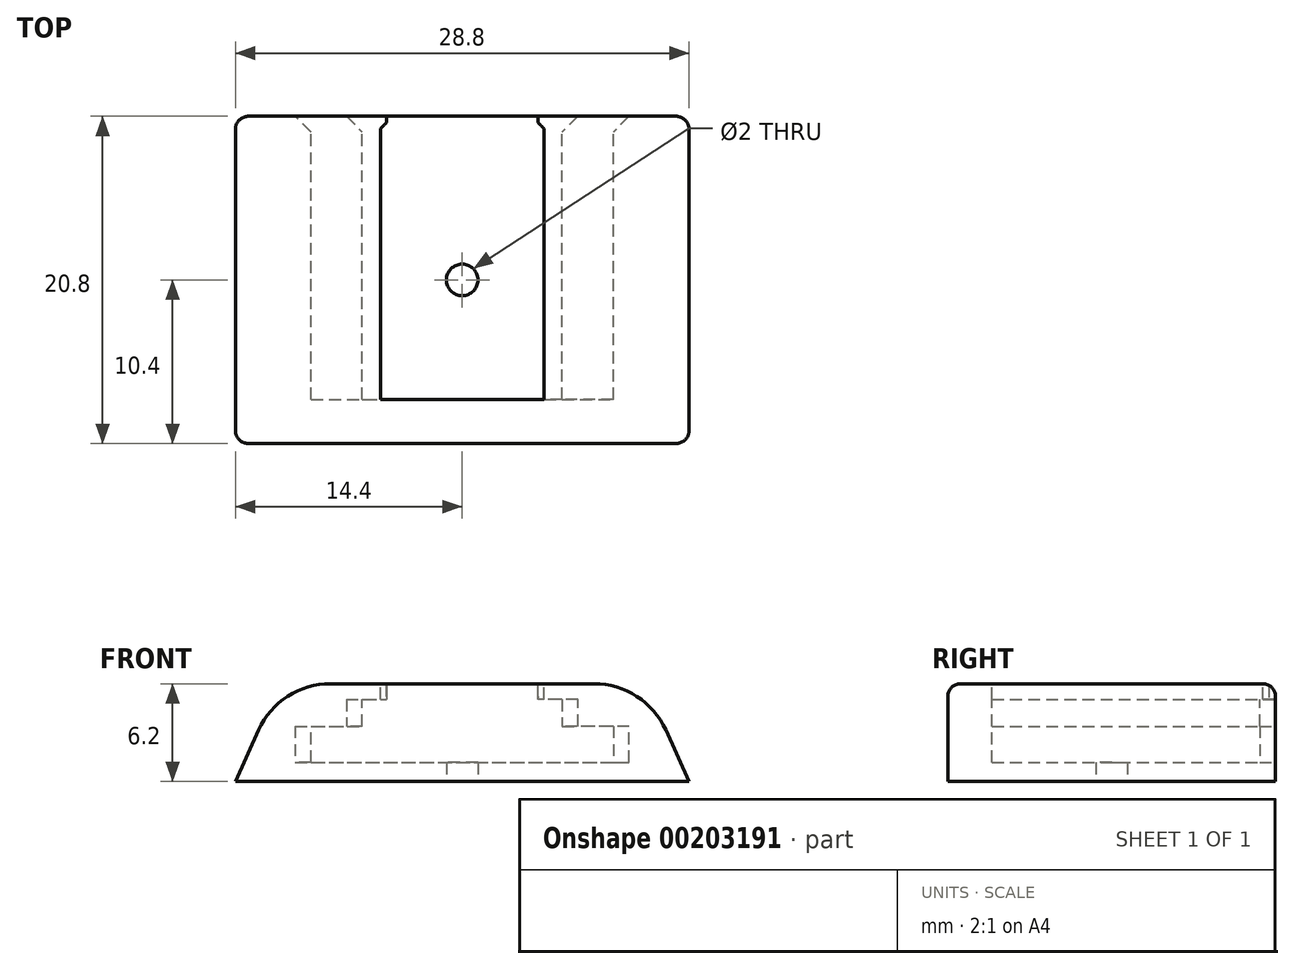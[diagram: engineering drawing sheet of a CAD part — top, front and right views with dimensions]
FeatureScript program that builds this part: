
annotation { "Feature Type Name" : "Feature", "Feature Type Description" : "" }
export const myFeature = defineFeature(function(context is Context, id is Id, definition is map)
    precondition{}
    {
        {
            var Q0;
            Q0=qCreatedBy(makeId("Front.planeOp"),FACE);
            var sketch = newSketch(context, id + "F0", { "sketchPlane" : qUnion([Q0])});
            skLineSegment(sketch, "E0", {"start": v(0, -5) * mm, "end": v(-9.6, -5) * mm});
            skLineSegment(sketch, "E1", {"start": v(-9.6, -5) * mm, "end": v(-9.6, -2.7) * mm});
            skLineSegment(sketch, "E2", {"start": v(-9.6, -2.7) * mm, "end": v(-6.35, -2.7) * mm});
            skLineSegment(sketch, "E3", {"start": v(-6.35, -2.7) * mm, "end": v(-6.35, -1) * mm});
            skLineSegment(sketch, "E4", {"start": v(-6.35, -1) * mm, "end": v(-5.2, -1) * mm});
            skLineSegment(sketch, "E5", {"start": v(-5.2, -1) * mm, "end": v(-5.2, 0) * mm});
            skLineSegment(sketch, "E6", {"start": v(-5.2, 0) * mm, "end": v(-11.6, 0) * mm});
            skLineSegment(sketch, "E7", {"start": v(-11.6, 0) * mm, "end": v(-14.4, -6.2) * mm});
            skLineSegment(sketch, "E8", {"start": v(-14.4, -6.2) * mm, "end": v(0, -6.2) * mm});
            skLineSegment(sketch, "E9.MirrorCS", {"start": v(14.4, -6.2) * mm, "end": v(0, -6.2) * mm});
            skLineSegment(sketch, "E10.MirrorCS", {"start": v(0, -5) * mm, "end": v(9.6, -5) * mm});
            skLineSegment(sketch, "E11.MirrorCS", {"start": v(9.6, -5) * mm, "end": v(9.6, -2.7) * mm});
            skLineSegment(sketch, "E12.MirrorCS", {"start": v(9.6, -2.7) * mm, "end": v(6.35, -2.7) * mm});
            skLineSegment(sketch, "E13.MirrorCS", {"start": v(6.35, -2.7) * mm, "end": v(6.35, -1) * mm});
            skLineSegment(sketch, "E14.MirrorCS", {"start": v(6.35, -1) * mm, "end": v(5.2, -1) * mm});
            skLineSegment(sketch, "E15.MirrorCS", {"start": v(5.2, -1) * mm, "end": v(5.2, 0) * mm});
            skLineSegment(sketch, "E16.MirrorCS", {"start": v(5.2, 0) * mm, "end": v(11.6, 0) * mm});
            skLineSegment(sketch, "E17.MirrorCS", {"start": v(11.6, 0) * mm, "end": v(14.4, -6.2) * mm});
            skLineSegment(sketch, "E18.bottom", {"start": v(5.2, 0) * mm, "end": v(4.8, 0) * mm});
            skLineSegment(sketch, "E18.top", {"start": v(5.2, -1) * mm, "end": v(4.8, -1) * mm});
            skLineSegment(sketch, "E18.left", {"start": v(5.2, 0) * mm, "end": v(5.2, -1) * mm});
            skLineSegment(sketch, "E18.right", {"start": v(4.8, 0) * mm, "end": v(4.8, -1) * mm});
            skLineSegment(sketch, "E19.MirrorCS", {"start": v(-4.8, 0) * mm, "end": v(-4.8, -1) * mm});
            skLineSegment(sketch, "E20.MirrorCS", {"start": v(-5.2, -1) * mm, "end": v(-4.8, -1) * mm});
            skLineSegment(sketch, "E21.MirrorCS", {"start": v(-5.2, 0) * mm, "end": v(-4.8, 0) * mm});
            skSolve(sketch);
        }
        {
            var Q0;
            Q0=makeQuery(id+"F0.imprint","IMPRINT",FACE,{"disambiguationData":[TD([[makeQuery(id+"F0.imprint","IMPRINT",EDGE,{"derivedFrom":sQuery(id+"F0.wireOp",EDGE,"E0")}),1.0]])]});
            extrude(context, id + "F1", {"entities" : qUnion([Q0]), "depth" : 20 * mm});
        }
        {
            var Q0;
            Q0=makeQuery(id+"F1.opExtrude","CAP_FACE",FACE,{"disambiguationData":[OSD([sQuery(id+"F0.wireOp",EDGE,"E0"),sQuery(id+"F0.wireOp",EDGE,"E1"),sQuery(id+"F0.wireOp",EDGE,"E2"),sQuery(id+"F0.wireOp",EDGE,"E3"),sQuery(id+"F0.wireOp",EDGE,"E4"),sQuery(id+"F0.wireOp",EDGE,"E5"),sQuery(id+"F0.wireOp",EDGE,"E6"),sQuery(id+"F0.wireOp",EDGE,"E7"),sQuery(id+"F0.wireOp",EDGE,"E8"),sQuery(id+"F0.wireOp",EDGE,"E9.MirrorCS"),sQuery(id+"F0.wireOp",EDGE,"E10.MirrorCS"),sQuery(id+"F0.wireOp",EDGE,"E11.MirrorCS"),sQuery(id+"F0.wireOp",EDGE,"E12.MirrorCS"),sQuery(id+"F0.wireOp",EDGE,"E13.MirrorCS"),sQuery(id+"F0.wireOp",EDGE,"E14.MirrorCS"),sQuery(id+"F0.wireOp",EDGE,"E15.MirrorCS"),sQuery(id+"F0.wireOp",EDGE,"E16.MirrorCS"),sQuery(id+"F0.wireOp",EDGE,"E17.MirrorCS")])],"isStart":false});
            var sketch = newSketch(context, id + "F2", { "sketchPlane" : qUnion([Q0])});
            skLineSegment(sketch, "E22.bottom", {"start": v(-14.4, 0) * mm, "end": v(11.6, 0) * mm});
            skLineSegment(sketch, "E22.top", {"start": v(-14.4, -6.2) * mm, "end": v(11.6, -6.2) * mm});
            skLineSegment(sketch, "E22.left", {"start": v(11.6, 0) * mm, "end": v(11.6, -6.2) * mm});
            skLineSegment(sketch, "E22.right", {"start": v(-14.4, 0) * mm, "end": v(-14.4, -6.2) * mm});
            skSolve(sketch);
        }
        {
            var Q0;
            Q0=makeQuery(id+"F2.imprint","IMPRINT",FACE,{"disambiguationData":[TD([[makeQuery(id+"F2.imprint","IMPRINT",EDGE,{"derivedFrom":sQuery(id+"F2.wireOp",EDGE,"E22.top")}),1.0]])]});
            var Q1;
            Q1=makeQuery(id+"F2.imprint","IMPRINT",FACE,{"disambiguationData":[TD([[makeQuery(id+"F2.imprint","IMPRINT",EDGE,{"derivedFrom":makeQuery(id+"F1.opExtrude","CAP_EDGE",EDGE,{"disambiguationData":[OSD([sQuery(id+"F0.wireOp",EDGE,"E1")])],"isStart":false})}),-1.0]])]});
            extrude(context, id + "F3", {"entities" : qUnion([Q0, Q1]), "operationType" : NewBodyOperationType.ADD, "oppositeDirection" : true, "depth" : 2 * mm});
        }
        {
            var Q0;
            Q0=makeQuery(id+"F0.imprint","IMPRINT",FACE,{"disambiguationData":[TD([[makeQuery(id+"F0.imprint","IMPRINT",EDGE,{"derivedFrom":sQuery(id+"F0.wireOp",EDGE,"E18.bottom")}),1.0]])]});
            var Q1;
            Q1=makeQuery(id+"F0.imprint","IMPRINT",FACE,{"disambiguationData":[TD([[makeQuery(id+"F0.imprint","IMPRINT",EDGE,{"derivedFrom":sQuery(id+"F0.wireOp",EDGE,"E5")}),-1.0]])]});
            var Q2;
            Q2=makeQuery(id+"F3.opExtrude","CAP_FACE",FACE,{"disambiguationData":[OSD([sQuery(id+"F2.wireOp",EDGE,"E22.bottom"),sQuery(id+"F2.wireOp",EDGE,"E22.top"),sQuery(id+"F2.wireOp",EDGE,"E22.left"),sQuery(id+"F2.wireOp",EDGE,"E22.right")])],"isStart":false});
            var Q3;
            Q3=makeQuery(id+"F3.boolean.opBoolean","MERGE",FACE,{"derivedFrom":[makeQuery(id+"F1.opExtrude","CAP_FACE",FACE,{"disambiguationData":[OSD([sQuery(id+"F0.wireOp",EDGE,"E0"),sQuery(id+"F0.wireOp",EDGE,"E1"),sQuery(id+"F0.wireOp",EDGE,"E2"),sQuery(id+"F0.wireOp",EDGE,"E3"),sQuery(id+"F0.wireOp",EDGE,"E4"),sQuery(id+"F0.wireOp",EDGE,"E5"),sQuery(id+"F0.wireOp",EDGE,"E6"),sQuery(id+"F0.wireOp",EDGE,"E7"),sQuery(id+"F0.wireOp",EDGE,"E8"),sQuery(id+"F0.wireOp",EDGE,"E9.MirrorCS"),sQuery(id+"F0.wireOp",EDGE,"E10.MirrorCS"),sQuery(id+"F0.wireOp",EDGE,"E11.MirrorCS"),sQuery(id+"F0.wireOp",EDGE,"E12.MirrorCS"),sQuery(id+"F0.wireOp",EDGE,"E13.MirrorCS"),sQuery(id+"F0.wireOp",EDGE,"E14.MirrorCS"),sQuery(id+"F0.wireOp",EDGE,"E16.MirrorCS"),sQuery(id+"F0.wireOp",EDGE,"E17.MirrorCS"),sQuery(id+"F0.wireOp",EDGE,"E18.left")])],"isStart":false}),makeQuery(id+"F3.opExtrude","CAP_FACE",FACE,{"disambiguationData":[OSD([sQuery(id+"F2.wireOp",EDGE,"E22.bottom"),sQuery(id+"F2.wireOp",EDGE,"E22.top"),sQuery(id+"F2.wireOp",EDGE,"E22.left"),sQuery(id+"F2.wireOp",EDGE,"E22.right")])],"isStart":true})]});
            extrude(context, id + "F4", {"entities" : qUnion([Q0, Q1, Q2, Q3]), "operationType" : NewBodyOperationType.ADD, "depth" : 0.8 * mm});
        }
        {
            var Q0;
            Q0=makeQuery(id+"F4.opExtrude","CAP_EDGE",EDGE,{"disambiguationData":[OSD([sQuery(id+"F0.wireOp",EDGE,"E19.MirrorCS")])],"isStart":false});
            var Q1;
            Q1=makeQuery(id+"F4.opExtrude","CAP_EDGE",EDGE,{"disambiguationData":[OSD([sQuery(id+"F0.wireOp",EDGE,"E18.right")])],"isStart":false});
            chamfer(context, id + "F5", {"entities" : qUnion([Q0, Q1]), "width" : 0.4 * mm, "tangentPropagation" : true});
        }
        {
            var Q0;
            {var subQ0=sQuery(id+"F0.wireOp",EDGE,"E17.MirrorCS");var subQ1=sQuery(id+"F0.wireOp",EDGE,"E16.MirrorCS");Q0=makeQuery(id+"F4.boolean.opBoolean","MERGE",EDGE,{"derivedFrom":[makeQuery(id+"F1.opExtrude","SWEPT_EDGE",EDGE,{"disambiguationData":[OSD([subQ1,subQ0])]}),makeQuery(id+"F4.opExtrude","SWEPT_EDGE",EDGE,{"disambiguationData":[OSD([subQ1,subQ0])]})]});}
            var Q1;
            {var subQ0=sQuery(id+"F0.wireOp",EDGE,"E7");var subQ1=sQuery(id+"F0.wireOp",EDGE,"E6");Q1=makeQuery(id+"F4.boolean.opBoolean","MERGE",EDGE,{"derivedFrom":[makeQuery(id+"F1.opExtrude","SWEPT_EDGE",EDGE,{"disambiguationData":[OSD([subQ1,subQ0])]}),makeQuery(id+"F4.opExtrude","SWEPT_EDGE",EDGE,{"disambiguationData":[OSD([subQ1,subQ0])]})]});}
            fillet(context, id + "F6", {"entities" : qUnion([Q0, Q1]), "radius" : 5 * mm, "tangentPropagation" : true, "allowEdgeOverflow" : false});
        }
        {
            var Q0;
            Q0=makeQuery(id+"F4.opExtrude","CAP_EDGE",EDGE,{"disambiguationData":[OSD([sQuery(id+"F0.wireOp",EDGE,"E17.MirrorCS")])],"isStart":false});
            var Q1;
            Q1=makeQuery(id+"F1.opExtrude","CAP_EDGE",EDGE,{"disambiguationData":[OSD([sQuery(id+"F0.wireOp",EDGE,"E17.MirrorCS")])],"isStart":true});
            var Q2;
            {var subQ0=sQuery(id+"F0.wireOp",EDGE,"E18.left");var subQ1=sQuery(id+"F0.wireOp",EDGE,"E5");var subQ2=sQuery(id+"F0.wireOp",EDGE,"E7");var subQ3=sQuery(id+"F0.wireOp",EDGE,"E6");Q2=makeQuery(id+"F6.opFillet","BLEND_EDGE",EDGE,{"blendedFrom":[makeQuery(id+"F4.boolean.opBoolean","MERGE",EDGE,{"derivedFrom":[makeQuery(id+"F1.opExtrude","SWEPT_EDGE",EDGE,{"disambiguationData":[OSD([subQ3,subQ2])]}),makeQuery(id+"F4.opExtrude","SWEPT_EDGE",EDGE,{"disambiguationData":[OSD([subQ3,subQ2])]})]}),makeQuery(id+"F4.boolean.opBoolean","MERGE",FACE,{"derivedFrom":[makeQuery(id+"F1.opExtrude","CAP_FACE",FACE,{"disambiguationData":[OSD([sQuery(id+"F0.wireOp",EDGE,"E0"),sQuery(id+"F0.wireOp",EDGE,"E1"),sQuery(id+"F0.wireOp",EDGE,"E2"),sQuery(id+"F0.wireOp",EDGE,"E3"),sQuery(id+"F0.wireOp",EDGE,"E4"),subQ1,subQ3,subQ2,sQuery(id+"F0.wireOp",EDGE,"E8"),sQuery(id+"F0.wireOp",EDGE,"E9.MirrorCS"),sQuery(id+"F0.wireOp",EDGE,"E10.MirrorCS"),sQuery(id+"F0.wireOp",EDGE,"E11.MirrorCS"),sQuery(id+"F0.wireOp",EDGE,"E12.MirrorCS"),sQuery(id+"F0.wireOp",EDGE,"E13.MirrorCS"),sQuery(id+"F0.wireOp",EDGE,"E14.MirrorCS"),sQuery(id+"F0.wireOp",EDGE,"E16.MirrorCS"),sQuery(id+"F0.wireOp",EDGE,"E17.MirrorCS"),subQ0])],"isStart":true}),makeQuery(id+"F4.opExtrude","CAP_FACE",FACE,{"disambiguationData":[OSD([subQ1,sQuery(id+"F0.wireOp",EDGE,"E19.MirrorCS"),sQuery(id+"F0.wireOp",EDGE,"E20.MirrorCS"),sQuery(id+"F0.wireOp",EDGE,"E21.MirrorCS")])],"isStart":true}),makeQuery(id+"F4.opExtrude","CAP_FACE",FACE,{"disambiguationData":[OSD([sQuery(id+"F0.wireOp",EDGE,"E18.bottom"),sQuery(id+"F0.wireOp",EDGE,"E18.top"),subQ0,sQuery(id+"F0.wireOp",EDGE,"E18.right")])],"isStart":true})]})],"blendedInto":[makeQuery(id+"F4.boolean.opBoolean","MERGE",FACE,{"derivedFrom":[makeQuery(id+"F1.opExtrude","CAP_FACE",FACE,{"disambiguationData":[OSD([sQuery(id+"F0.wireOp",EDGE,"E0"),sQuery(id+"F0.wireOp",EDGE,"E1"),sQuery(id+"F0.wireOp",EDGE,"E2"),sQuery(id+"F0.wireOp",EDGE,"E3"),sQuery(id+"F0.wireOp",EDGE,"E4"),subQ1,subQ3,subQ2,sQuery(id+"F0.wireOp",EDGE,"E8"),sQuery(id+"F0.wireOp",EDGE,"E9.MirrorCS"),sQuery(id+"F0.wireOp",EDGE,"E10.MirrorCS"),sQuery(id+"F0.wireOp",EDGE,"E11.MirrorCS"),sQuery(id+"F0.wireOp",EDGE,"E12.MirrorCS"),sQuery(id+"F0.wireOp",EDGE,"E13.MirrorCS"),sQuery(id+"F0.wireOp",EDGE,"E14.MirrorCS"),sQuery(id+"F0.wireOp",EDGE,"E16.MirrorCS"),sQuery(id+"F0.wireOp",EDGE,"E17.MirrorCS"),subQ0])],"isStart":true}),makeQuery(id+"F4.opExtrude","CAP_FACE",FACE,{"disambiguationData":[OSD([subQ1,sQuery(id+"F0.wireOp",EDGE,"E19.MirrorCS"),sQuery(id+"F0.wireOp",EDGE,"E20.MirrorCS"),sQuery(id+"F0.wireOp",EDGE,"E21.MirrorCS")])],"isStart":true}),makeQuery(id+"F4.opExtrude","CAP_FACE",FACE,{"disambiguationData":[OSD([sQuery(id+"F0.wireOp",EDGE,"E18.bottom"),sQuery(id+"F0.wireOp",EDGE,"E18.top"),subQ0,sQuery(id+"F0.wireOp",EDGE,"E18.right")])],"isStart":true})]})]});}
            fillet(context, id + "F7", {"entities" : qUnion([Q0, Q1, Q2]), "radius" : 0.8 * mm, "tangentPropagation" : true, "allowEdgeOverflow" : false});
        }
        {
            var Q0;
            Q0=makeQuery(id+"F1.opExtrude","CAP_EDGE",EDGE,{"disambiguationData":[OSD([sQuery(id+"F0.wireOp",EDGE,"E1")])],"isStart":true});
            var Q1;
            Q1=makeQuery(id+"F1.opExtrude","CAP_EDGE",EDGE,{"disambiguationData":[OSD([sQuery(id+"F0.wireOp",EDGE,"E3")])],"isStart":true});
            var Q2;
            Q2=makeQuery(id+"F1.opExtrude","CAP_EDGE",EDGE,{"disambiguationData":[OSD([sQuery(id+"F0.wireOp",EDGE,"E13.MirrorCS")])],"isStart":true});
            var Q3;
            Q3=makeQuery(id+"F1.opExtrude","CAP_EDGE",EDGE,{"disambiguationData":[OSD([sQuery(id+"F0.wireOp",EDGE,"E11.MirrorCS")])],"isStart":true});
            chamfer(context, id + "F8", {"entities" : qUnion([Q0, Q1, Q2, Q3]), "width" : 1 * mm, "tangentPropagation" : true});
        }
        {
            var Q0;
            {var subQ0=sQuery(id+"F0.wireOp",EDGE,"E9.MirrorCS");var subQ1=sQuery(id+"F0.wireOp",EDGE,"E8");Q0=makeQuery(id+"F4.boolean.opBoolean","MERGE",FACE,{"derivedFrom":[makeQuery(id+"F1.opExtrude","SWEPT_FACE",FACE,{"disambiguationData":[OSD([subQ1,subQ0])]}),makeQuery(id+"F4.opExtrude","SWEPT_FACE",FACE,{"disambiguationData":[OSD([subQ1,subQ0])]})]});}
            var sketch = newSketch(context, id + "F9", { "sketchPlane" : qUnion([Q0])});
            skPoint(sketch, "E23", {"position": v(0, 10.4) * mm});
            skLineSegment(sketch, "E24", {"start": v(0, 20.8) * mm, "end": v(0, 0) * mm, "construction": true});
            skCircle(sketch, "E25", {"center": v(0, 10.4) * mm, "radius": 1 * mm});
            skSolve(sketch);
        }
        {
            var Q0;
            Q0=makeQuery(id+"F9.imprint","IMPRINT",FACE,{"disambiguationData":[TD([[makeQuery(id+"F9.imprint","IMPRINT",EDGE,{"derivedFrom":sQuery(id+"F9.wireOp",EDGE,"E25")}),1.0]])]});
            extrude(context, id + "F10", {"entities" : qUnion([Q0]), "operationType" : NewBodyOperationType.REMOVE, "endBound" : BoundingType.UP_TO_NEXT, "oppositeDirection" : true, "depth" : 25 * mm});
        }
    });
